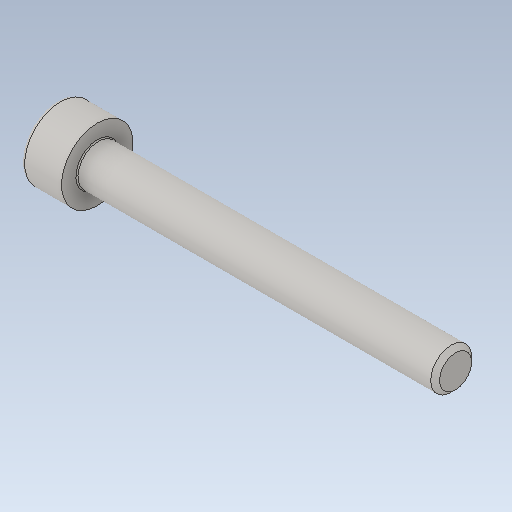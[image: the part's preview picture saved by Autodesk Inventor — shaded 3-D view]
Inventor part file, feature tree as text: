
AUTODESK INVENTOR PART (.ipt)
format: ipt  version: 2020.2 (Build 242310000, 310)  size: 118,272 bytes
history: imported  units: mm
features: imported_body x1
ambient origin geometry x8: Origin, YZ Plane, XZ Plane, XY Plane, X Axis, Y Axis, Z Axis, Center Point
bodies: Solide1 (imported_parasolid), Solid1 (imported_parasolid)
feature tree (1):
  imported_body  NMx_Import_Brep_tag  [imported B-rep: ~11 faces, bbox_mm=[38.6, 5.5, 0.0]]
